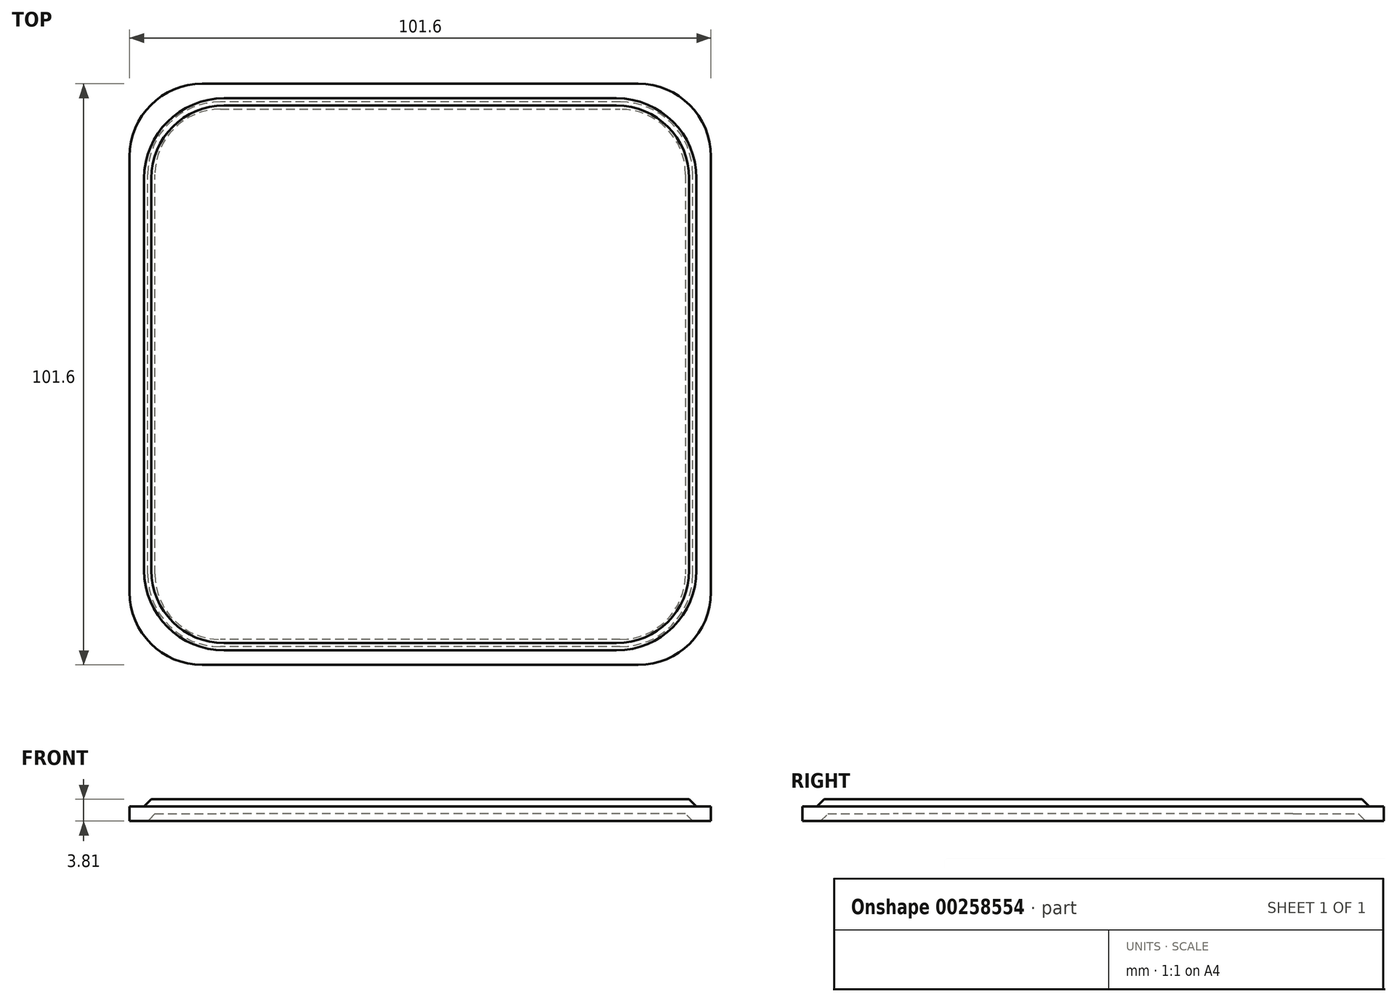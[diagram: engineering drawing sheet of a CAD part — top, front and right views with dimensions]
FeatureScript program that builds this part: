
annotation { "Feature Type Name" : "Feature", "Feature Type Description" : "" }
export const myFeature = defineFeature(function(context is Context, id is Id, definition is map)
    precondition{}
    {
        {
            var Q0;
            Q0=qCreatedBy(makeId("Top.planeOp"),FACE);
            var sketch = newSketch(context, id + "F0", { "sketchPlane" : qUnion([Q0])});
            skLineSegment(sketch, "E0.bottom", {"start": v(38.1, 50.8) * mm, "end": v(-38.1, 50.8) * mm});
            skLineSegment(sketch, "E0.top", {"start": v(38.1, -50.8) * mm, "end": v(-38.1, -50.8) * mm});
            skLineSegment(sketch, "E0.left", {"start": v(50.8, 38.1) * mm, "end": v(50.8, -38.1) * mm});
            skLineSegment(sketch, "E0.right", {"start": v(-50.8, 38.1) * mm, "end": v(-50.8, -38.1) * mm});
            skPoint(sketch, "E0.middle", {"position": v(0, 0) * mm});
            skPoint(sketch, "E1.visualSharp", {"position": v(-50.8, 50.8) * mm});
            skArc(sketch, "E1.filletArc", {"start": v(-38.1, 50.8) * mm, "mid": v(-47.08, 47.08) * mm, "end": v(-50.8, 38.1) * mm});
            skPoint(sketch, "E2.visualSharp", {"position": v(50.8, 50.8) * mm});
            skArc(sketch, "E2.filletArc", {"start": v(50.8, 38.1) * mm, "mid": v(47.08, 47.08) * mm, "end": v(38.1, 50.8) * mm});
            skPoint(sketch, "E3.visualSharp", {"position": v(50.8, -50.8) * mm});
            skArc(sketch, "E3.filletArc", {"start": v(38.1, -50.8) * mm, "mid": v(47.08, -47.08) * mm, "end": v(50.8, -38.1) * mm});
            skPoint(sketch, "E4.visualSharp", {"position": v(-50.8, -50.8) * mm});
            skArc(sketch, "E4.filletArc", {"start": v(-50.8, -38.1) * mm, "mid": v(-47.08, -47.08) * mm, "end": v(-38.1, -50.8) * mm});
            skSolve(sketch);
        }
        {
            var Q0;
            Q0=makeQuery(id+"F0.imprint","IMPRINT",FACE,{"disambiguationData":[TD([[makeQuery(id+"F0.imprint","IMPRINT",EDGE,{"derivedFrom":sQuery(id+"F0.wireOp",EDGE,"E0.bottom")}),1.0]])]});
            extrude(context, id + "F1", {"entities" : qUnion([Q0]), "depth" : 2.54 * mm});
        }
        {
            var Q0;
            Q0=makeQuery(id+"F1.opExtrude","CAP_FACE",FACE,{"disambiguationData":[OSD([sQuery(id+"F0.wireOp",EDGE,"E0.bottom"),sQuery(id+"F0.wireOp",EDGE,"E0.top"),sQuery(id+"F0.wireOp",EDGE,"E0.left"),sQuery(id+"F0.wireOp",EDGE,"E0.right"),sQuery(id+"F0.wireOp",EDGE,"E1.filletArc"),sQuery(id+"F0.wireOp",EDGE,"E2.filletArc"),sQuery(id+"F0.wireOp",EDGE,"E3.filletArc"),sQuery(id+"F0.wireOp",EDGE,"E4.filletArc")])],"isStart":true});
            var sketch = newSketch(context, id + "F2", { "sketchPlane" : qUnion([Q0])});
            skLineSegment(sketch, "E5.bottom", {"start": v(34.93, 47.63) * mm, "end": v(-34.92, 47.63) * mm});
            skLineSegment(sketch, "E5.top", {"start": v(34.93, -47.63) * mm, "end": v(-34.93, -47.63) * mm});
            skLineSegment(sketch, "E5.left", {"start": v(47.63, 34.93) * mm, "end": v(47.63, -34.93) * mm});
            skLineSegment(sketch, "E5.right", {"start": v(-47.63, 34.93) * mm, "end": v(-47.63, -34.93) * mm});
            skPoint(sketch, "E5.middle", {"position": v(0, 0) * mm});
            skPoint(sketch, "E6.visualSharp", {"position": v(47.63, 47.63) * mm});
            skArc(sketch, "E6.filletArc", {"start": v(47.63, 34.93) * mm, "mid": v(43.9, 43.9) * mm, "end": v(34.93, 47.63) * mm});
            skPoint(sketch, "E7.visualSharp", {"position": v(47.63, -47.63) * mm});
            skArc(sketch, "E7.filletArc", {"start": v(34.93, -47.63) * mm, "mid": v(43.9, -43.9) * mm, "end": v(47.63, -34.93) * mm});
            skPoint(sketch, "E8.visualSharp", {"position": v(-47.63, -47.63) * mm});
            skArc(sketch, "E8.filletArc", {"start": v(-47.63, -34.93) * mm, "mid": v(-43.9, -43.9) * mm, "end": v(-34.93, -47.63) * mm});
            skPoint(sketch, "E9.visualSharp", {"position": v(-47.63, 47.63) * mm});
            skArc(sketch, "E9.filletArc", {"start": v(-34.92, 47.63) * mm, "mid": v(-43.9, 43.9) * mm, "end": v(-47.62, 34.93) * mm});
            skSolve(sketch);
        }
        {
            var Q0;
            Q0=makeQuery(id+"F2.imprint","IMPRINT",FACE,{"disambiguationData":[TD([[makeQuery(id+"F2.imprint","IMPRINT",EDGE,{"derivedFrom":sQuery(id+"F2.wireOp",EDGE,"E5.bottom")}),-1.0]])]});
            extrude(context, id + "F3", {"entities" : qUnion([Q0]), "operationType" : NewBodyOperationType.ADD, "depth" : 1.27 * mm});
        }
        {
            var Q0;
            Q0=makeQuery(id+"F1.opExtrude","CAP_FACE",FACE,{"disambiguationData":[OSD([sQuery(id+"F0.wireOp",EDGE,"E0.bottom"),sQuery(id+"F0.wireOp",EDGE,"E0.top"),sQuery(id+"F0.wireOp",EDGE,"E0.left"),sQuery(id+"F0.wireOp",EDGE,"E0.right"),sQuery(id+"F0.wireOp",EDGE,"E1.filletArc"),sQuery(id+"F0.wireOp",EDGE,"E2.filletArc"),sQuery(id+"F0.wireOp",EDGE,"E3.filletArc"),sQuery(id+"F0.wireOp",EDGE,"E4.filletArc")])],"isStart":false});
            var sketch = newSketch(context, id + "F4", { "sketchPlane" : qUnion([Q0])});
            skLineSegment(sketch, "E10.bottom", {"start": v(34.3, -46.99) * mm, "end": v(-34.3, -47) * mm});
            skLineSegment(sketch, "E10.top", {"start": v(34.3, 47) * mm, "end": v(-34.3, 46.99) * mm});
            skLineSegment(sketch, "E10.left", {"start": v(47, -34.29) * mm, "end": v(47, 34.3) * mm});
            skLineSegment(sketch, "E10.right", {"start": v(-47, -34.3) * mm, "end": v(-47, 34.29) * mm});
            skPoint(sketch, "E10.middle", {"position": v(0, 0) * mm});
            skPoint(sketch, "E11.visualSharp", {"position": v(-47, -47) * mm});
            skArc(sketch, "E11.filletArc", {"start": v(-47, -34.3) * mm, "mid": v(-43.27, -43.27) * mm, "end": v(-34.3, -47) * mm});
            skPoint(sketch, "E12.visualSharp", {"position": v(47, -46.99) * mm});
            skArc(sketch, "E12.filletArc", {"start": v(34.3, -46.99) * mm, "mid": v(43.27, -43.27) * mm, "end": v(47, -34.29) * mm});
            skPoint(sketch, "E13.visualSharp", {"position": v(47, 47) * mm});
            skArc(sketch, "E13.filletArc", {"start": v(47, 34.3) * mm, "mid": v(43.27, 43.27) * mm, "end": v(34.3, 47) * mm});
            skPoint(sketch, "E14.visualSharp", {"position": v(-46.99, 46.99) * mm});
            skArc(sketch, "E14.filletArc", {"start": v(-34.3, 46.99) * mm, "mid": v(-43.27, 43.27) * mm, "end": v(-47, 34.29) * mm});
            skSolve(sketch);
        }
        {
            var Q0;
            Q0=makeQuery(id+"F4.imprint","IMPRINT",FACE,{"disambiguationData":[TD([[makeQuery(id+"F4.imprint","IMPRINT",EDGE,{"derivedFrom":sQuery(id+"F4.wireOp",EDGE,"E10.bottom")}),1.0]])]});
            extrude(context, id + "F5", {"entities" : qUnion([Q0]), "operationType" : NewBodyOperationType.REMOVE, "oppositeDirection" : true, "depth" : 1.27 * mm});
        }
        {
            var Q0;
            Q0=makeQuery(id+"F5.boolean.opBoolean","COPY",EDGE,{"derivedFrom":makeQuery(id+"F5.opExtrude","CAP_EDGE",EDGE,{"disambiguationData":[OSD([sQuery(id+"F4.wireOp",EDGE,"E10.top")])],"isStart":false})});
            var Q1;
            Q1=makeQuery(id+"F5.boolean.opBoolean","COPY",EDGE,{"derivedFrom":makeQuery(id+"F5.opExtrude","CAP_EDGE",EDGE,{"disambiguationData":[OSD([sQuery(id+"F4.wireOp",EDGE,"E14.filletArc")])],"isStart":false})});
            var Q2;
            Q2=makeQuery(id+"F5.boolean.opBoolean","COPY",EDGE,{"derivedFrom":makeQuery(id+"F5.opExtrude","CAP_EDGE",EDGE,{"disambiguationData":[OSD([sQuery(id+"F4.wireOp",EDGE,"E10.right")])],"isStart":false})});
            var Q3;
            Q3=makeQuery(id+"F5.boolean.opBoolean","COPY",EDGE,{"derivedFrom":makeQuery(id+"F5.opExtrude","CAP_EDGE",EDGE,{"disambiguationData":[OSD([sQuery(id+"F4.wireOp",EDGE,"E11.filletArc")])],"isStart":false})});
            chamfer(context, id + "F6", {"entities" : qUnion([Q0, Q1, Q2, Q3]), "width" : 1.27 * mm, "tangentPropagation" : true});
        }
        {
            var Q0;
            Q0=makeQuery(id+"F1.opExtrude","CAP_FACE",FACE,{"disambiguationData":[OSD([sQuery(id+"F0.wireOp",EDGE,"E0.bottom"),sQuery(id+"F0.wireOp",EDGE,"E0.top"),sQuery(id+"F0.wireOp",EDGE,"E0.left"),sQuery(id+"F0.wireOp",EDGE,"E0.right"),sQuery(id+"F0.wireOp",EDGE,"E1.filletArc"),sQuery(id+"F0.wireOp",EDGE,"E2.filletArc"),sQuery(id+"F0.wireOp",EDGE,"E3.filletArc"),sQuery(id+"F0.wireOp",EDGE,"E4.filletArc")])],"isStart":true});
            chamfer(context, id + "F7", {"entities" : qUnion([Q0]), "width" : 1.27 * mm, "tangentPropagation" : true});
        }
    });
